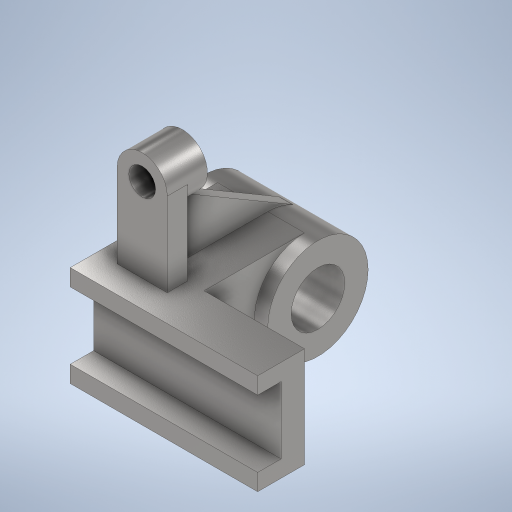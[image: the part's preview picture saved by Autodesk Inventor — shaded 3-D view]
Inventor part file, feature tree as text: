
AUTODESK INVENTOR PART (.ipt)
format: ipt  version: 2024 (Build 280153000, 153)  size: 373,248 bytes
history: native  units: mm
features: extrude x8, sketch x6, plane x3, projected_geometry x1
ambient origin geometry x8: Origin, YZ Plane, XZ Plane, XY Plane, X Axis, Y Axis, Z Axis, Center Point
bodies: Volumenkörper1 (feature_tree)
feature tree (18):
  extrude  "Extrusion1"  Depth=112.0mm
  extrude  "Extrusion2"  Depth=40.0mm
  extrude  "Extrusion3"  Depth=14.0mm
  plane  "Arbeitsebene1"
  sketch  "Skizze7"  dims[d7=60.0mm d8=0.0mm d9=60.0mm]
  extrude  "Extrusion6"  Depth=60.0mm
  extrude  "Extrusion7"  Depth=60.0mm
  plane  "Arbeitsebene2"
  sketch  "Skizze11"  dims[d11=60.0mm d12=0.0mm d21=60.0mm]
  extrude  "Extrusion10"  Depth=8.0mm
  extrude  "Extrusion11"  Depth=60.0mm
  plane  "Arbeitsebene3"
  extrude  "Extrusion12"  Depth=68.0mm TaperAngle=0.0deg
  sketch  "Skizze1"  dims[d0=28.0mm d1=112.0mm]
  sketch  "Skizze2"  dims[d2=60.0mm d3=0.0mm d4=40.0mm]
  sketch  "Skizze3"  dims[d5=10.0mm d6=14.0mm]
  sketch  "Skizze13"  dims[d25=60.0mm d26=32.0mm d27=60.0mm d28=68.0mm d29=0.0mm d30=68.0mm d31=0.0mm d32=16.0mm d42=30.0mm d43=16.0mm d44=10.0mm d45=50.0mm d46=24.0mm d47=0.0mm d48=12.0mm d49=0.0mm d50=30.0mm d53=8.0mm d54=0.0mm d55=5.323254mm d56=66.0mm d57=72.0mm d58=3.0mm]
  projected_geometry  "Projizierte Kontur1"
